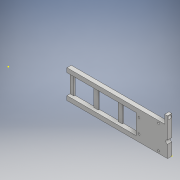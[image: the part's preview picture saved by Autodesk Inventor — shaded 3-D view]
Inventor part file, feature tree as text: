
AUTODESK INVENTOR PART (.ipt)
format: ipt  version: 2018 (Build 220112000, 112)  size: 498,688 bytes
history: native  units: mm
features: sketch x41, extrude x31, hole x8, fillet x6
ambient origin geometry x8: Origin, YZ Plane, XZ Plane, XY Plane, X Axis, Y Axis, Z Axis, Center Point
bodies: Solid1 (feature_tree)
feature tree (86):
  extrude  "Extrusion1"  Depth=50.0mm
  hole  "Hole1"  [1 undecoded]
  hole  "Hole2"  [1 undecoded]
  extrude  "Extrusion2"  Depth=2.0mm
  extrude  "Extrusion3"  Depth=2.0mm
  extrude  "Extrusion4"  Depth=5.0mm
  sketch  "Sketch7"  dims[d25=10.0mm d26=5.0mm]
  extrude  "Extrusion5"  Depth=5.0mm
  extrude  "Extrusion6"  Depth=35.0mm
  extrude  "Extrusion7"  Depth=35.0mm
  extrude  "Extrusion8"  Depth=35.0mm
  extrude  "Extrusion9"  Depth=2.0mm TaperAngle=0.0deg
  extrude  "Extrusion10"  Depth=7.5mm TaperAngle=0.0deg
  extrude  "Extrusion11"  Depth=10.0mm
  extrude  "Extrusion12"  Depth=7.5mm
  fillet  "Fillet1"  Radius=7.5mm
  fillet  "Fillet2"  Radius=25.0mm
  fillet  "Fillet3"  Radius=3.0mm
  fillet  "Fillet4"  Radius=3.2mm
  fillet  "Fillet5"  Radius=2.1mm
  fillet  "Fillet6"  Radius=5.5mm
  extrude  "Extrusion13"  Depth=92.5mm TaperAngle=0.0deg
  sketch  "Sketch17"  dims[d58=4.25mm d59=241.0mm d60=0.0mm]
  hole  "Hole3"  [1 undecoded]
  hole  "Hole4"  [1 undecoded]
  extrude  "Extrusion14"  Depth=5.0mm
  extrude  "Extrusion15"  Depth=2.5mm TaperAngle=0.0deg
  extrude  "Extrusion16"  Depth=30.0mm
  extrude  "Extrusion17"  Depth=2.5mm
  extrude  "Extrusion18"  Depth=14.55mm TaperAngle=0.0deg
  extrude  "Extrusion19"  Depth=0.1mm
  extrude  "Extrusion20"  Depth=3.25mm
  extrude  "Extrusion21"  Depth=3.25mm
  hole  "Hole5"  [1 undecoded]
  extrude  "Extrusion22"  Depth=2.0mm
  extrude  "Extrusion23"  Depth=15.0mm
  extrude  "Extrusion24"  Depth=10.0mm TaperAngle=0.0deg
  hole  "Hole6"  [1 undecoded]
  extrude  "Extrusion25"  Depth=100.0mm TaperAngle=0.0deg
  extrude  "Extrusion26"  Depth=2.0mm TaperAngle=0.0deg
  extrude  "Extrusion27"  Depth=3.3mm
  extrude  "Extrusion28"  Depth=3.3mm
  hole  "Hole7"  [1 undecoded]
  extrude  "Extrusion29"  Depth=2.0mm
  extrude  "Extrusion30"  Depth=21.0mm
  hole  "Hole8"  [1 undecoded]
  extrude  "Extrusion31"  Depth=15.0mm
  sketch  "Sketch1"  dims[d0=50.0mm d1=50.0mm]
  sketch  "Sketch2"  dims[d2=240.0mm d3=7.5mm]
  sketch  "Sketch3"  dims[d4=7.5mm d5=7.5mm d6=0.0mm]
  sketch  "Sketch4"  dims[d7=6.35mm d8=6.0mm d9=4.0mm d10=2.0mm d11=90.0deg d12=8.0mm d13=20.594885mm d14=25.0mm]
  sketch  "Sketch5"  dims[d15=3.3mm d16=6.0mm d17=4.0mm d18=2.0mm d19=90.0deg d20=8.0mm d21=20.594885mm d22=25.0mm]
  sketch  "Sketch6"  dims[d23=180.0deg d24=5.0mm]
  sketch  "Sketch8"  dims[d27=17.5mm d28=0.0mm d30=35.0mm]
  sketch  "Sketch9"  dims[d31=35.0mm d32=35.0mm]
  sketch  "Sketch10"  dims[d33=35.0mm d34=35.0mm]
  sketch  "Sketch11"  dims[d35=35.0mm d36=2.0mm d37=0.0mm]
  sketch  "Sketch12"  dims[d38=10.0mm d39=7.5mm d40=0.0mm]
  sketch  "Sketch13"  dims[d41=100.0mm d42=10.0mm]
  sketch  "Sketch14"  dims[d43=7.5mm d44=0.0mm d45=7.5mm d46=7.5mm d47=25.0mm d48=0.0mm d49=3.0mm d50=3.2mm d51=2.1mm d52=5.5mm]
  sketch  "Sketch15"  dims[d53=3.3mm d54=92.5mm d55=0.0mm]
  sketch  "Sketch16"  dims[d56=5.5mm d57=3.3mm]
  sketch  "Sketch18"  dims[d61=4.44mm d62=5.0mm]
  sketch  "Sketch19"  dims[d63=2.5mm d64=91.25mm d65=0.0mm]
  sketch  "Sketch20"  dims[d66=30.0mm d67=6.35mm]
  sketch  "Sketch21"  dims[d68=3.8mm d69=0.0mm d70=2.5mm]
  sketch  "Sketch22"  dims[d71=14.55mm d72=0.0mm d73=14.55mm d74=0.0mm]
  sketch  "Sketch23"  dims[d75=0.1mm d76=0.1mm]
  sketch  "Sketch24"  dims[d77=3.25mm d78=3.25mm]
  sketch  "Sketch25"  dims[d79=3.25mm d80=3.25mm]
  sketch  "Sketch26"  dims[d81=35.0mm d82=10.0mm]
  sketch  "Sketch27"  dims[d83=2.0mm d84=0.0mm d85=3.6mm]
  sketch  "Sketch28"  dims[d86=3.6mm]
  sketch  "Sketch29"  dims[d87=3.3mm d88=6.0mm d89=4.0mm d90=2.0mm d91=90.0deg d92=15.0mm d93=20.594885mm]
  sketch  "Sketch30"  dims[d94=3.3mm d95=6.0mm d96=4.0mm d97=2.0mm d98=90.0deg d99=15.0mm d100=20.594885mm d101=6.0mm]
  sketch  "Sketch31"  dims[d102=20.0mm d103=0.0mm d104=10.0mm d105=0.0mm]
  sketch  "Sketch32"  dims[d106=2.0mm d107=0.0mm d108=4.0mm]
  sketch  "Sketch33"  dims[d109=100.0mm d110=0.0mm d111=100.0mm d112=0.0mm]
  sketch  "Sketch34"  dims[d113=5.0mm d114=2.0mm d115=0.0mm]
  sketch  "Sketch35"  dims[d116=3.3mm d117=3.3mm]
  sketch  "Sketch36"  dims[d118=3.3mm d119=3.3mm]
  sketch  "Sketch37"  dims[d120=2.0mm d121=0.0mm d122=5.5mm d123=0.0mm]
  sketch  "Sketch38"  dims[d124=3.3mm d125=6.0mm d126=4.0mm d127=2.0mm d128=90.0deg d129=8.0mm d130=20.594885mm d131=42.0mm]
  sketch  "Sketch39"  dims[d132=17.0mm d133=21.0mm]
  sketch  "Sketch40"  dims[d135=8.5mm d136=15.825mm]
  sketch  "Sketch41"  dims[d137=3.5mm d138=21.0mm d139=3.3mm d140=3.3mm d141=3.3mm d142=10.0mm d143=0.0mm d144=7.5mm d145=0.0mm d146=5.0mm d147=10.0mm d148=5.0mm d149=10.0mm d150=17.5mm d151=0.0mm d152=5.0mm d153=7.0mm d154=6.0mm d155=4.0mm d156=2.0mm d157=90.0deg d158=8.0mm d159=20.594885mm d160=17.5mm d161=0.0mm d162=170.5mm d163=0.0mm d164=3.75mm d165=3.75mm d166=3.75mm d167=3.75mm d168=10.0mm d169=0.0mm d170=100.0mm d171=0.0mm d172=5.0mm d173=6.0mm d174=4.0mm d175=2.0mm d176=90.0deg d177=15.0mm d178=0.0mm d179=2.0mm d180=0.0mm d181=5.0mm d182=15.0mm d183=0.0mm d184=7.5mm d185=6.0mm d186=6.0mm d187=4.0mm d188=2.0mm d189=90.0deg d190=15.0mm d191=0.0mm d192=17.5mm d193=0.0mm]
note: 8 required parameter values undecoded (feature->parameter linkage not recoverable at this tier; creation-order binding heuristic only, values carry confidence <= 0.55)
